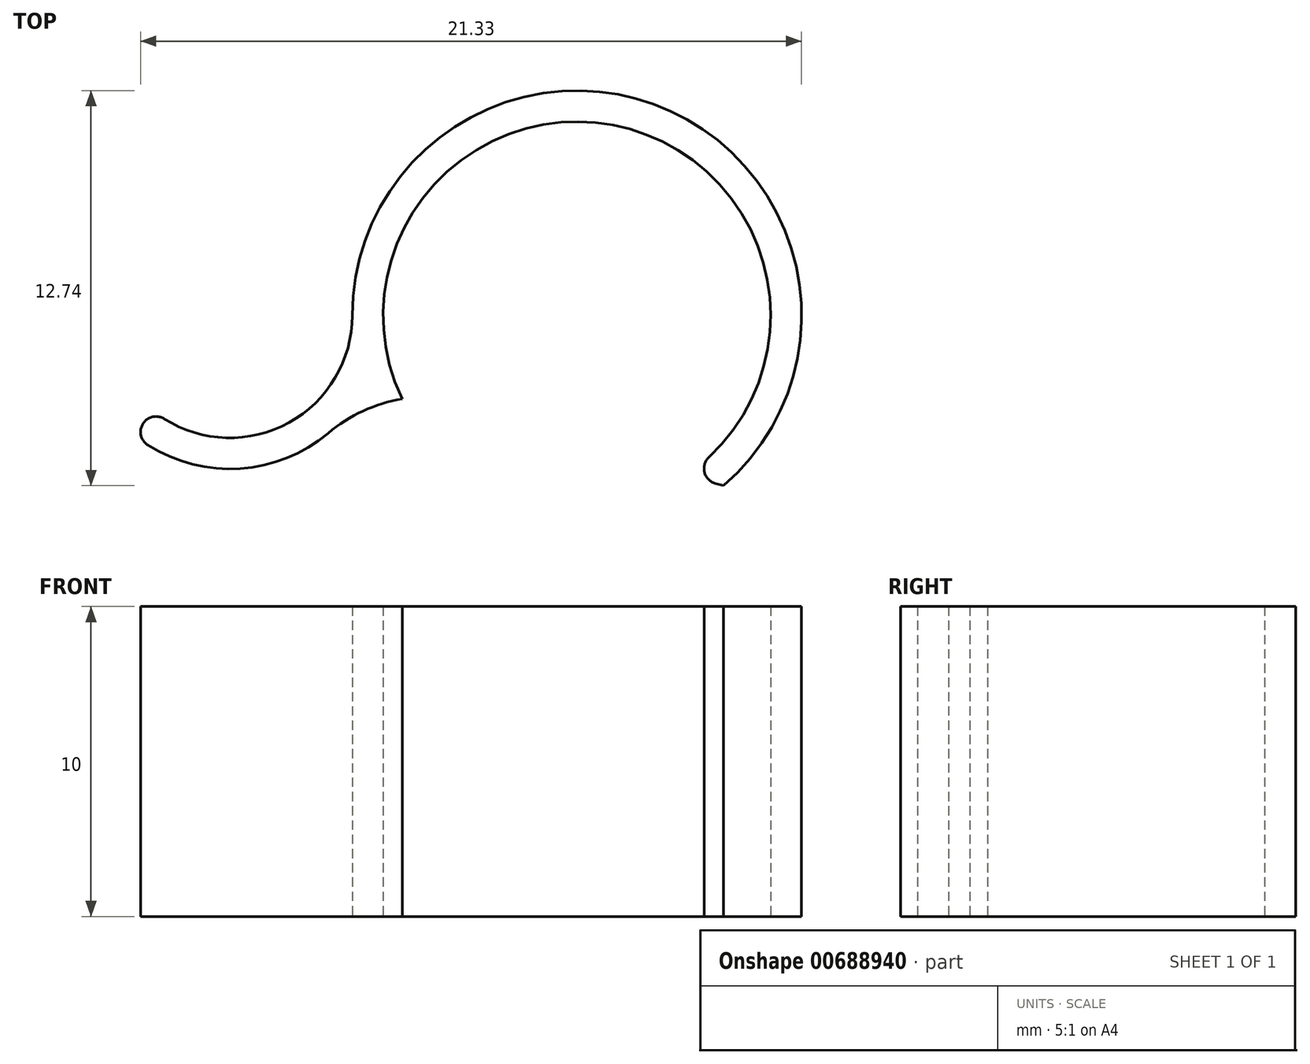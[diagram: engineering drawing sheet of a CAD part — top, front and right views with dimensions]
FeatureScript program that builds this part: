
annotation { "Feature Type Name" : "Feature", "Feature Type Description" : "" }
export const myFeature = defineFeature(function(context is Context, id is Id, definition is map)
    precondition{}
    {
        {
            var Q0;
            Q0=qCreatedBy(makeId("Top.planeOp"),FACE);
            var sketch = newSketch(context, id + "F0", { "sketchPlane" : qUnion([Q0])});
            skCircle(sketch, "E0", {"center": v(0, 0) * mm, "radius": 3.95 * mm});
            skCircle(sketch, "E1", {"center": v(0, 0) * mm, "radius": 4.95 * mm});
            skCircle(sketch, "E2", {"center": v(11.2, 0) * mm, "radius": 6.25 * mm});
            skCircle(sketch, "E3", {"center": v(11.2, 0) * mm, "radius": 7.25 * mm});
            skLineSegment(sketch, "E4", {"start": v(4.35, -2.37) * mm, "end": v(15.93, -5.5) * mm});
            skLineSegment(sketch, "E5", {"start": v(4.35, -2.37) * mm, "end": v(-3.58, -3.41) * mm});
            skSolve(sketch);
        }
        {
            var Q0;
            {var subQ0=sQuery(id+"F0.wireOp",EDGE,"E5");var subQ1=sQuery(id+"F0.wireOp",EDGE,"E0");var subQ2=makeQuery(id+"F0.imprint","INTERSECT",VERTEX,{"disambiguationData":[OD(0.0)],"derivedFrom":[subQ1,subQ0]});Q0=makeQuery(id+"F0.imprint","IMPRINT",FACE,{"disambiguationData":[TD([[makeQuery(id+"F0.imprint","IMPRINT",EDGE,{"disambiguationData":[TD([[subQ2,1.0]])],"derivedFrom":subQ1}),-1.0]])]});}
            var Q1;
            {var subQ0=sQuery(id+"F0.wireOp",EDGE,"E3");var subQ1=sQuery(id+"F0.wireOp",EDGE,"E1");var subQ2=makeQuery(id+"F0.imprint","INTERSECT",VERTEX,{"derivedFrom":[subQ1,subQ0]});Q1=makeQuery(id+"F0.imprint","IMPRINT",FACE,{"disambiguationData":[TD([[makeQuery(id+"F0.imprint","IMPRINT",EDGE,{"disambiguationData":[TD([[subQ2,1.0]])],"derivedFrom":subQ1}),1.0]])]});}
            var Q2;
            {var subQ0=sQuery(id+"F0.wireOp",EDGE,"E3");var subQ1=sQuery(id+"F0.wireOp",EDGE,"E0");var subQ2=makeQuery(id+"F0.imprint","INTERSECT",VERTEX,{"derivedFrom":[subQ1,subQ0]});Q2=makeQuery(id+"F0.imprint","IMPRINT",FACE,{"disambiguationData":[TD([[makeQuery(id+"F0.imprint","IMPRINT",EDGE,{"disambiguationData":[TD([[subQ2,1.0]])],"derivedFrom":subQ1}),-1.0]])]});}
            var Q3;
            {var subQ1=sQuery(id+"F0.wireOp",EDGE,"E1");var subQ3=sQuery(id+"F0.wireOp",EDGE,"E2");var subQ4=makeQuery(id+"F0.imprint","INTERSECT",VERTEX,{"derivedFrom":[subQ1,subQ3]});Q3=makeQuery(id+"F0.imprint","IMPRINT",FACE,{"disambiguationData":[TD([[makeQuery(id+"F0.imprint","IMPRINT",EDGE,{"disambiguationData":[TD([[subQ4,-1.0]])],"derivedFrom":subQ3}),-1.0]])]});}
            var Q4;
            {var subQ0=sQuery(id+"F0.wireOp",EDGE,"E3");var subQ1=sQuery(id+"F0.wireOp",EDGE,"E1");var subQ2=makeQuery(id+"F0.imprint","INTERSECT",VERTEX,{"derivedFrom":[subQ1,subQ0]});Q4=makeQuery(id+"F0.imprint","IMPRINT",FACE,{"disambiguationData":[TD([[makeQuery(id+"F0.imprint","IMPRINT",EDGE,{"disambiguationData":[TD([[subQ2,1.0]])],"derivedFrom":subQ1}),-1.0]])]});}
            extrude(context, id + "F1", {"entities" : qUnion([Q0, Q1, Q2, Q3, Q4]), "depth" : 10 * mm, "offsetDistance" : 25 * mm});
        }
        {
            var Q0;
            Q0=makeQuery(id+"F1.opExtrude","SWEPT_EDGE",EDGE,{"disambiguationData":[OSD([sQuery(id+"F0.wireOp",EDGE,"E1"),sQuery(id+"F0.wireOp",EDGE,"E3")])]});
            fillet(context, id + "F2", {"entities" : qUnion([Q0]), "radius" : 5 * mm, "tangentPropagation" : true, "allowEdgeOverflow" : false});
        }
        {
            var Q0;
            Q0=makeQuery(id+"F1.opExtrude","SWEPT_EDGE",EDGE,{"disambiguationData":[OSD([sQuery(id+"F0.wireOp",EDGE,"E1"),sQuery(id+"F0.wireOp",EDGE,"E5")])]});
            var Q1;
            {var subQ0=sQuery(id+"F0.wireOp",EDGE,"E5");var subQ1=sQuery(id+"F0.wireOp",EDGE,"E0");Q1=makeQuery(id+"F1.opExtrude","SWEPT_EDGE",EDGE,{"disambiguationData":[OSD([subQ1,subQ0]),TDD([makeQuery(id+"F0.imprint","INTERSECT",VERTEX,{"disambiguationData":[OD(0.0)],"derivedFrom":[subQ1,subQ0]})])]});}
            var Q2;
            {var subQ0=sQuery(id+"F0.wireOp",EDGE,"E5");var subQ1=sQuery(id+"F0.wireOp",EDGE,"E0");Q2=makeQuery(id+"F1.opExtrude","SWEPT_EDGE",EDGE,{"disambiguationData":[OSD([subQ1,subQ0]),TDD([makeQuery(id+"F0.imprint","INTERSECT",VERTEX,{"disambiguationData":[OD(1.0)],"derivedFrom":[subQ1,subQ0]})])]});}
            var Q3;
            {var subQ0=sQuery(id+"F0.wireOp",EDGE,"E4");var subQ1=sQuery(id+"F0.wireOp",EDGE,"E2");Q3=makeQuery(id+"F1.opExtrude","SWEPT_EDGE",EDGE,{"disambiguationData":[OSD([subQ1,subQ0]),TDD([makeQuery(id+"F0.imprint","INTERSECT",VERTEX,{"disambiguationData":[OD(0.0)],"derivedFrom":[subQ1,subQ0]})])]});}
            var Q4;
            {var subQ0=sQuery(id+"F0.wireOp",EDGE,"E4");var subQ1=sQuery(id+"F0.wireOp",EDGE,"E2");Q4=makeQuery(id+"F1.opExtrude","SWEPT_EDGE",EDGE,{"disambiguationData":[OSD([subQ1,subQ0]),TDD([makeQuery(id+"F0.imprint","INTERSECT",VERTEX,{"disambiguationData":[OD(1.0)],"derivedFrom":[subQ1,subQ0]})])]});}
            fillet(context, id + "F3", {"entities" : qUnion([Q0, Q1, Q2, Q3, Q4]), "radius" : .5 * mm, "tangentPropagation" : true, "allowEdgeOverflow" : false});
        }
    });
